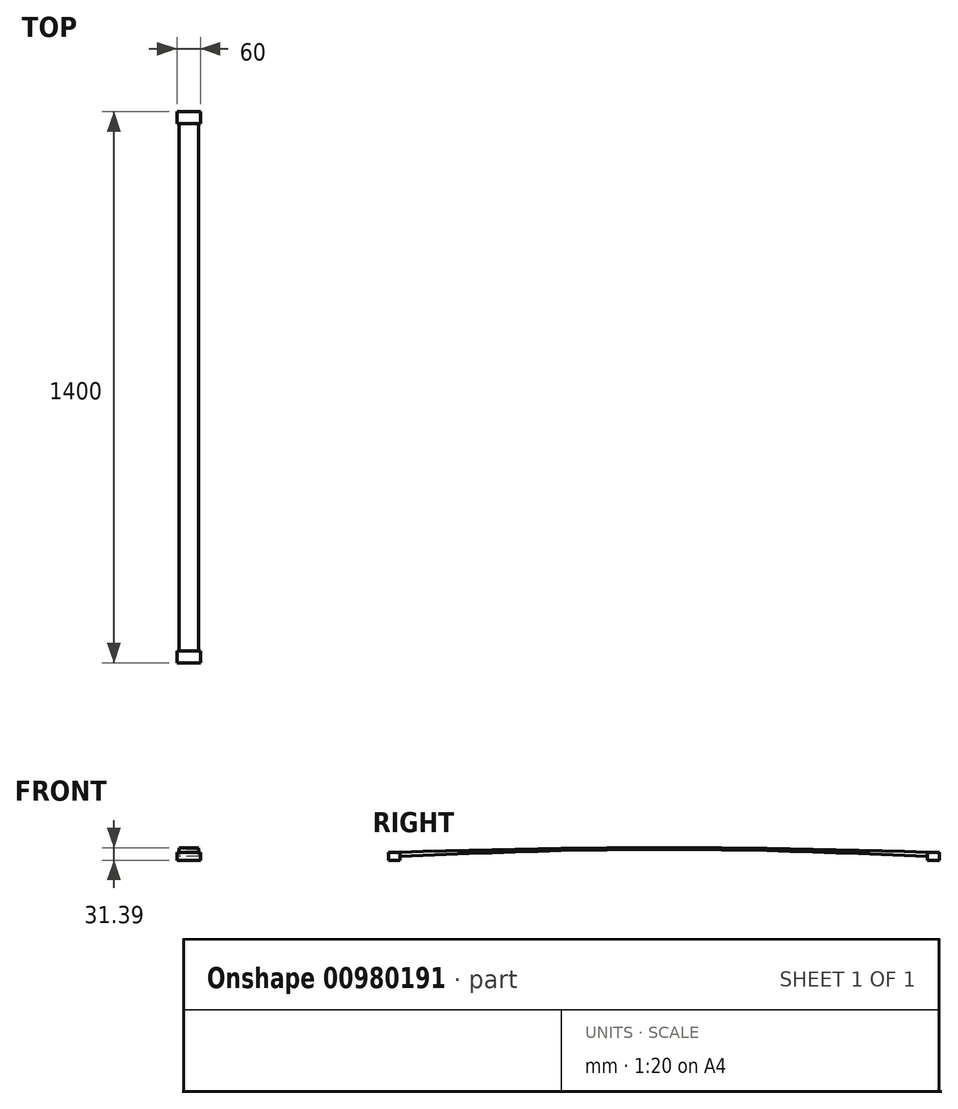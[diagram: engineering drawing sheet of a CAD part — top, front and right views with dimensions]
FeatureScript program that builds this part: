
annotation { "Feature Type Name" : "Feature", "Feature Type Description" : "" }
export const myFeature = defineFeature(function(context is Context, id is Id, definition is map)
    precondition{}
    {
        {
            var Q0;
            Q0=qCreatedBy(makeId("Right.planeOp"),FACE);
            var sketch = newSketch(context, id + "F0", { "sketchPlane" : qUnion([Q0])});
            skLineSegment(sketch, "E0.bottom", {"start": v(700, 10) * mm, "end": v(670, 10) * mm});
            skLineSegment(sketch, "E0.top", {"start": v(700, -10) * mm, "end": v(670, -10) * mm});
            skLineSegment(sketch, "E0.left", {"start": v(700, 10) * mm, "end": v(700, -10) * mm});
            skLineSegment(sketch, "E0.right", {"start": v(-700, 10) * mm, "end": v(-700, -10) * mm});
            skPoint(sketch, "E0.middle", {"position": v(0, 0) * mm});
            skLineSegment(sketch, "E1.left", {"start": v(-670, 10) * mm, "end": v(-670, -10) * mm});
            skLineSegment(sketch, "E1.right", {"start": v(670, 10) * mm, "end": v(670, -10) * mm});
            skLineSegment(sketch, "E2.trimOffspring", {"start": v(-670, -10) * mm, "end": v(-700, -10) * mm});
            skLineSegment(sketch, "E3.trimOffspring", {"start": v(-670, 10) * mm, "end": v(-700, 10) * mm});
            skFitSpline(sketch, "E4", {"points": [v(-670, 10) * mm, v(670, 10) * mm], "startDerivative": vector(1344.5, 45.57) * mm, "endDerivative": vector(1339.3, -45.57) * mm});
            skFitSpline(sketch, "E5.0", {"points": [v(-669.66, 0) * mm, v(-221.72, 15.19) * mm, v(223.45, 15.19) * mm, v(669.66, 0) * mm]});
            skLineSegment(sketch, "E6", {"start": v(669.66, 0) * mm, "end": v(670, 0) * mm});
            skLineSegment(sketch, "E7", {"start": v(-669.66, 0) * mm, "end": v(-670, 0) * mm});
            skSolve(sketch);
        }
        {
            var Q0;
            {var subQ0=sQuery(id+"F0.wireOp",EDGE,"E4");Q0=makeQuery(id+"F0.imprint","IMPRINT",FACE,{"disambiguationData":[TD([[makeQuery(id+"F0.imprint","IMPRINT",EDGE,{"derivedFrom":subQ0}),-1.0]])]});}
            extrude(context, id + "F1", {"entities" : qUnion([Q0]), "endBound" : BoundingType.SYMMETRIC, "depth" : 50 * mm, "offsetDistance" : 25 * mm});
        }
        {
            var Q0;
            Q0=makeQuery(id+"F0.imprint","IMPRINT",FACE,{"disambiguationData":[TD([[makeQuery(id+"F0.imprint","IMPRINT",EDGE,{"derivedFrom":sQuery(id+"F0.wireOp",EDGE,"E0.right")}),1.0]])]});
            var Q1;
            {var subQ1=sQuery(id+"F0.wireOp",EDGE,"E0.bottom");Q1=makeQuery(id+"F0.imprint","IMPRINT",FACE,{"disambiguationData":[TD([[makeQuery(id+"F0.imprint","IMPRINT",EDGE,{"derivedFrom":subQ1}),1.0]])]});}
            extrude(context, id + "F2", {"entities" : qUnion([Q0, Q1]), "operationType" : NewBodyOperationType.ADD, "endBound" : BoundingType.SYMMETRIC, "depth" : 60 * mm, "offsetDistance" : 25 * mm});
        }
    });
